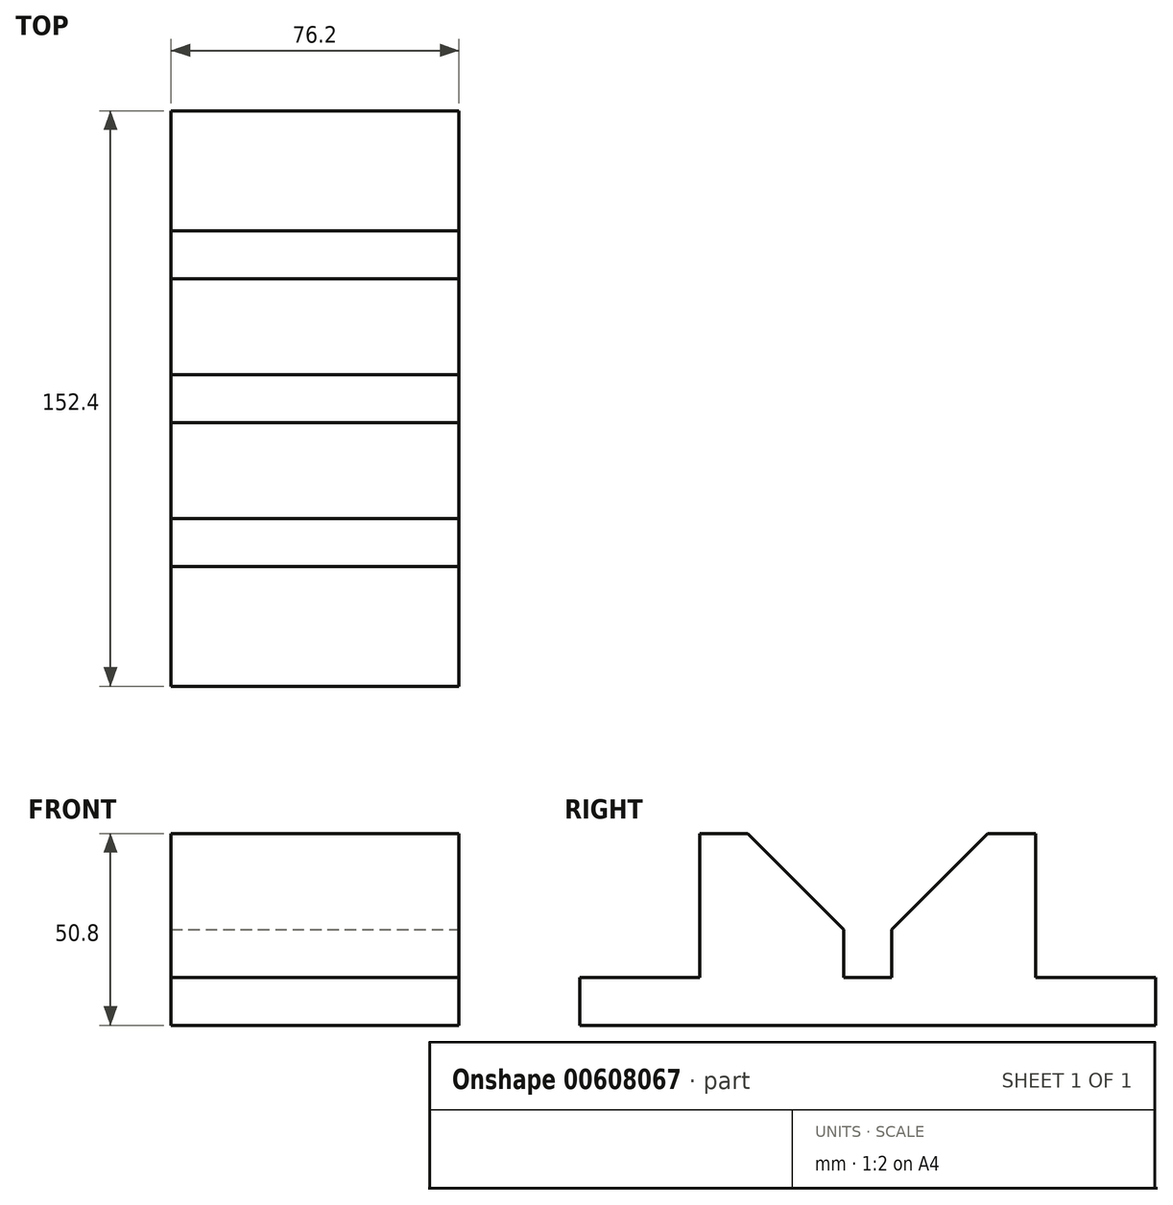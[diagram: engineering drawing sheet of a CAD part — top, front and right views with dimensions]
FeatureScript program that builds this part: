
annotation { "Feature Type Name" : "Feature", "Feature Type Description" : "" }
export const myFeature = defineFeature(function(context is Context, id is Id, definition is map)
    precondition{}
    {
        {
            var Q0;
            Q0=qCreatedBy(makeId("Front.planeOp"),FACE);
            var sketch = newSketch(context, id + "F0", { "sketchPlane" : qUnion([Q0])});
            skLineSegment(sketch, "E0.bottom", {"start": v(0, 0) * mm, "end": v(76.2, 0) * mm});
            skLineSegment(sketch, "E0.top", {"start": v(0, 12.7) * mm, "end": v(76.2, 12.7) * mm});
            skLineSegment(sketch, "E0.left", {"start": v(0, 0) * mm, "end": v(0, 12.7) * mm});
            skLineSegment(sketch, "E0.right", {"start": v(76.2, 0) * mm, "end": v(76.2, 12.7) * mm});
            skSolve(sketch);
        }
        {
            var Q0;
            Q0=makeQuery(id+"F0.imprint","IMPRINT",FACE,{"disambiguationData":[TD([[makeQuery(id+"F0.imprint","IMPRINT",EDGE,{"derivedFrom":sQuery(id+"F0.wireOp",EDGE,"E0.bottom")}),1.0]])]});
            extrude(context, id + "F1", {"entities" : qUnion([Q0]), "oppositeDirection" : true, "depth" : 152.4 * mm, "offsetDistance" : 25.4 * mm});
        }
        {
            var Q0;
            Q0=makeQuery(id+"F1.opExtrude","SWEPT_FACE",FACE,{"disambiguationData":[OSD([sQuery(id+"F0.wireOp",EDGE,"E0.top")])]});
            var sketch = newSketch(context, id + "F2", { "sketchPlane" : qUnion([Q0])});
            skLineSegment(sketch, "E1.bottom", {"start": v(0, 120.65) * mm, "end": v(76.2, 120.65) * mm});
            skLineSegment(sketch, "E1.top", {"start": v(0, 82.55) * mm, "end": v(76.2, 82.55) * mm});
            skLineSegment(sketch, "E1.left", {"start": v(0, 120.65) * mm, "end": v(0, 82.55) * mm});
            skLineSegment(sketch, "E1.right", {"start": v(76.2, 120.65) * mm, "end": v(76.2, 82.55) * mm});
            skLineSegment(sketch, "E2.bottom", {"start": v(0, 69.85) * mm, "end": v(76.2, 69.85) * mm});
            skLineSegment(sketch, "E2.top", {"start": v(0, 31.75) * mm, "end": v(76.2, 31.75) * mm});
            skLineSegment(sketch, "E2.left", {"start": v(0, 69.85) * mm, "end": v(0, 31.75) * mm});
            skLineSegment(sketch, "E2.right", {"start": v(76.2, 69.85) * mm, "end": v(76.2, 31.75) * mm});
            skSolve(sketch);
        }
        {
            var Q0;
            Q0=makeQuery(id+"F2.imprint","IMPRINT",FACE,{"disambiguationData":[TD([[makeQuery(id+"F2.imprint","IMPRINT",EDGE,{"derivedFrom":sQuery(id+"F2.wireOp",EDGE,"E1.bottom")}),-1.0]])]});
            var Q1;
            Q1=makeQuery(id+"F2.imprint","IMPRINT",FACE,{"disambiguationData":[TD([[makeQuery(id+"F2.imprint","IMPRINT",EDGE,{"derivedFrom":sQuery(id+"F2.wireOp",EDGE,"E2.bottom")}),-1.0]])]});
            extrude(context, id + "F3", {"entities" : qUnion([Q0, Q1]), "operationType" : NewBodyOperationType.ADD, "depth" : 38.1 * mm, "offsetDistance" : 25.4 * mm});
        }
        {
            var Q0;
            Q0=makeQuery(id+"F3.boolean.opBoolean","MERGE",FACE,{"derivedFrom":[makeQuery(id+"F1.opExtrude","SWEPT_FACE",FACE,{"disambiguationData":[OSD([sQuery(id+"F0.wireOp",EDGE,"E0.right")])]}),makeQuery(id+"F3.opExtrude","SWEPT_FACE",FACE,{"disambiguationData":[OSD([sQuery(id+"F2.wireOp",EDGE,"E1.right")])]}),makeQuery(id+"F3.opExtrude","SWEPT_FACE",FACE,{"disambiguationData":[OSD([sQuery(id+"F2.wireOp",EDGE,"E2.right")])]})]});
            var sketch = newSketch(context, id + "F4", { "sketchPlane" : qUnion([Q0])});
            skLineSegment(sketch, "E3", {"start": v(44.45, 50.8) * mm, "end": v(69.85, 25.4) * mm});
            skLineSegment(sketch, "E4", {"start": v(107.95, 50.8) * mm, "end": v(82.55, 25.4) * mm});
            skSolve(sketch);
        }
        {
            var Q0;
            {var subQ0=sQuery(id+"F4.wireOp",EDGE,"E3");Q0=makeQuery(id+"F4.imprint","IMPRINT",FACE,{"disambiguationData":[TD([[makeQuery(id+"F4.imprint","IMPRINT",EDGE,{"derivedFrom":subQ0}),1.0]])]});}
            var Q1;
            {var subQ0=sQuery(id+"F4.wireOp",EDGE,"E4");Q1=makeQuery(id+"F4.imprint","IMPRINT",FACE,{"disambiguationData":[TD([[makeQuery(id+"F4.imprint","IMPRINT",EDGE,{"derivedFrom":subQ0}),-1.0]])]});}
            extrude(context, id + "F5", {"entities" : qUnion([Q0, Q1]), "operationType" : NewBodyOperationType.REMOVE, "oppositeDirection" : true, "depth" : 76.2 * mm, "offsetDistance" : 25.4 * mm});
        }
    });
